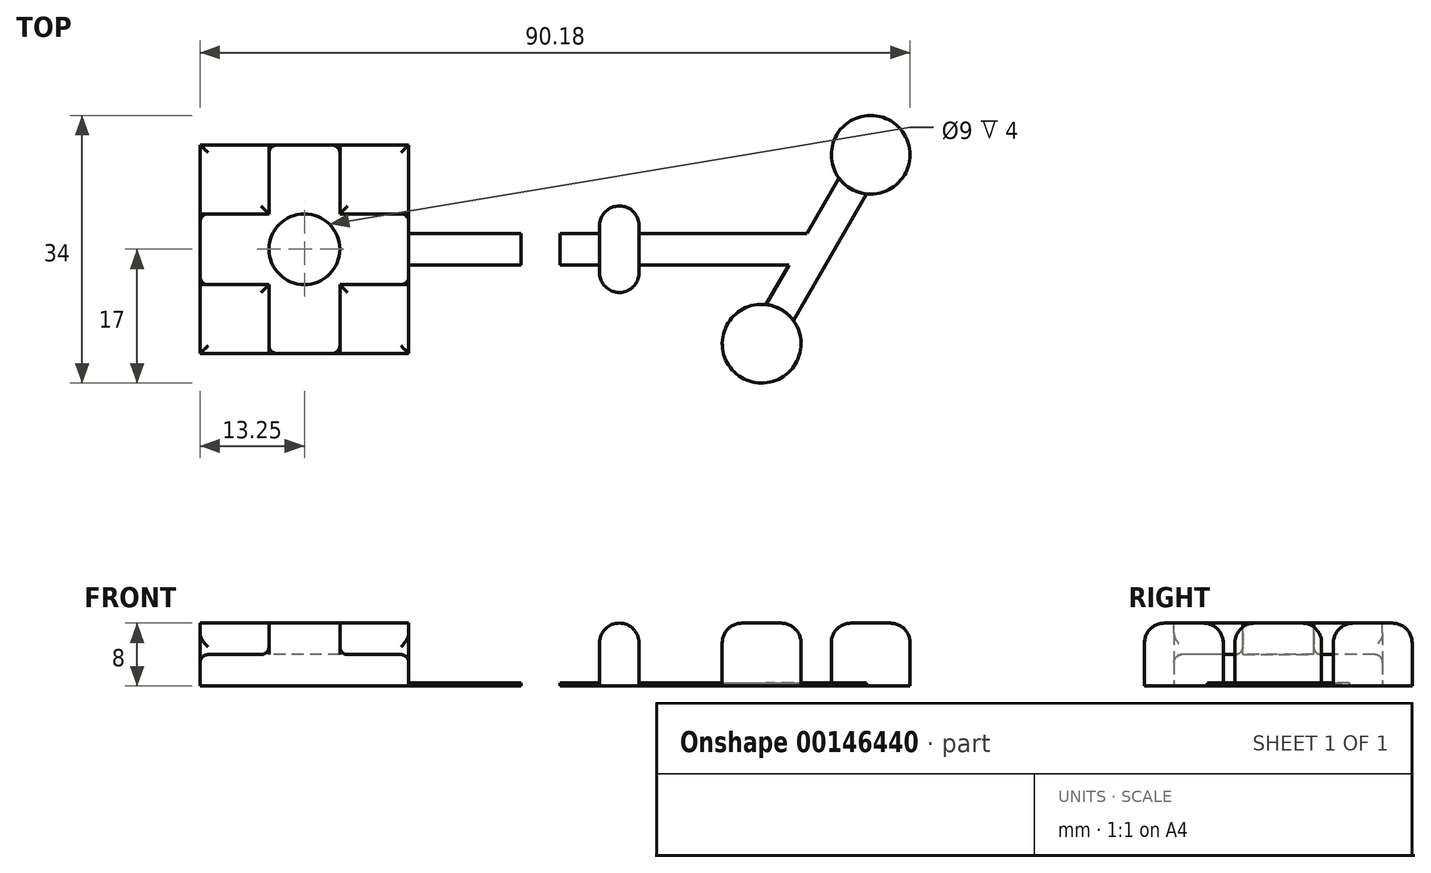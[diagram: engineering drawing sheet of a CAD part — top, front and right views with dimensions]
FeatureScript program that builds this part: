
annotation { "Feature Type Name" : "Feature", "Feature Type Description" : "" }
export const myFeature = defineFeature(function(context is Context, id is Id, definition is map)
    precondition{}
    {
        {
            var Q0;
            Q0=qCreatedBy(makeId("Top.planeOp"),FACE);
            var sketch = newSketch(context, id + "F0", { "sketchPlane" : qUnion([Q0])});
            skLineSegment(sketch, "E0.bottom", {"start": v(13.25, 13.25) * mm, "end": v(-13.25, 13.25) * mm});
            skLineSegment(sketch, "E0.top", {"start": v(13.25, -13.25) * mm, "end": v(-13.25, -13.25) * mm});
            skLineSegment(sketch, "E0.left", {"start": v(13.25, 13.25) * mm, "end": v(13.25, -13.25) * mm});
            skLineSegment(sketch, "E0.right", {"start": v(-13.25, 13.25) * mm, "end": v(-13.25, -13.25) * mm});
            skPoint(sketch, "E0.middle", {"position": v(0, 0) * mm});
            skLineSegment(sketch, "E1", {"start": v(0, 0) * mm, "end": v(65, 0) * mm, "construction": true});
            skLineSegment(sketch, "E2", {"start": v(58.07, -12) * mm, "end": v(71.93, 12) * mm, "construction": true});
            skPoint(sketch, "E3", {"position": v(58.07, -12) * mm});
            skCircle(sketch, "E4", {"center": v(71.93, 12) * mm, "radius": 5 * mm});
            skCircle(sketch, "E5", {"center": v(58.07, -12) * mm, "radius": 5 * mm});
            skLineSegment(sketch, "E6.bottom", {"start": v(32.5, -3) * mm, "end": v(27.5, -3) * mm, "construction": true});
            skLineSegment(sketch, "E6.top", {"start": v(32.5, 3) * mm, "end": v(27.5, 3) * mm, "construction": true});
            skLineSegment(sketch, "E6.left", {"start": v(32.5, -3) * mm, "end": v(32.5, 3) * mm});
            skLineSegment(sketch, "E6.right", {"start": v(27.5, -3) * mm, "end": v(27.5, 3) * mm});
            skPoint(sketch, "E6.middle", {"position": v(30, 0) * mm});
            skLineSegment(sketch, "E7.bottom", {"start": v(42.5, -3) * mm, "end": v(37.5, -3) * mm, "construction": true});
            skLineSegment(sketch, "E7.top", {"start": v(42.5, 3) * mm, "end": v(37.5, 3) * mm, "construction": true});
            skLineSegment(sketch, "E7.left", {"start": v(42.5, -3) * mm, "end": v(42.5, 3) * mm});
            skLineSegment(sketch, "E7.right", {"start": v(37.5, -3) * mm, "end": v(37.5, 3) * mm});
            skPoint(sketch, "E7.middle", {"position": v(40, 0) * mm});
            skArc(sketch, "E8", {"start": v(27.5, 3) * mm, "mid": v(30, 5.5) * mm, "end": v(32.5, 3) * mm});
            skArc(sketch, "E9", {"start": v(27.5, -3) * mm, "mid": v(30, -5.5) * mm, "end": v(32.5, -3) * mm});
            skArc(sketch, "E10", {"start": v(37.5, -3) * mm, "mid": v(40, -5.5) * mm, "end": v(42.5, -3) * mm});
            skArc(sketch, "E11", {"start": v(37.5, 3) * mm, "mid": v(40, 5.5) * mm, "end": v(42.5, 3) * mm});
            skLineSegment(sketch, "E12.0", {"start": v(58.63, -7.03) * mm, "end": v(67.9, 9.03) * mm});
            skLineSegment(sketch, "E13.MirrorCS", {"start": v(62.1, -9.03) * mm, "end": v(71.37, 7.03) * mm});
            skLineSegment(sketch, "E14", {"start": v(13.25, 2) * mm, "end": v(27.5, 2) * mm});
            skLineSegment(sketch, "E15", {"start": v(32.5, 2) * mm, "end": v(37.5, 2) * mm});
            skLineSegment(sketch, "E16", {"start": v(42.5, 2) * mm, "end": v(63.85, 2) * mm});
            skLineSegment(sketch, "E17.MirrorCS", {"start": v(13.25, -2) * mm, "end": v(27.5, -2) * mm});
            skLineSegment(sketch, "E18.MirrorCS", {"start": v(32.5, -2) * mm, "end": v(37.5, -2) * mm});
            skLineSegment(sketch, "E19.MirrorCS", {"start": v(42.5, -2) * mm, "end": v(61.54, -2) * mm});
            skPoint(sketch, "E20.orphan", {"position": v(63.85, -2) * mm});
            skSolve(sketch);
        }
        {
            var Q0;
            {var subQ3=sQuery(id+"F0.wireOp",EDGE,"E0.bottom");Q0=makeQuery(id+"F0.imprint","IMPRINT",FACE,{"disambiguationData":[TD([[makeQuery(id+"F0.imprint","IMPRINT",EDGE,{"derivedFrom":subQ3}),1.0]])]});}
            var Q1;
            {var subQ0=sQuery(id+"F0.wireOp",EDGE,"E4");var subQ1=makeQuery(id+"F0.imprint","INTERSECT",VERTEX,{"derivedFrom":[subQ0,sQuery(id+"F0.wireOp",EDGE,"E12.0")]});Q1=makeQuery(id+"F0.imprint","IMPRINT",FACE,{"disambiguationData":[TD([[makeQuery(id+"F0.imprint","IMPRINT",EDGE,{"disambiguationData":[TD([[subQ1,-1.0]])],"derivedFrom":subQ0}),1.0]])]});}
            var Q2;
            {var subQ0=sQuery(id+"F0.wireOp",EDGE,"E5");var subQ1=makeQuery(id+"F0.imprint","INTERSECT",VERTEX,{"derivedFrom":[subQ0,sQuery(id+"F0.wireOp",EDGE,"E12.0")]});Q2=makeQuery(id+"F0.imprint","IMPRINT",FACE,{"disambiguationData":[TD([[makeQuery(id+"F0.imprint","IMPRINT",EDGE,{"disambiguationData":[TD([[subQ1,1.0]])],"derivedFrom":subQ0}),1.0]])]});}
            var Q3;
            {var subQ3=sQuery(id+"F0.wireOp",EDGE,"E8");Q3=makeQuery(id+"F0.imprint","IMPRINT",FACE,{"disambiguationData":[TD([[makeQuery(id+"F0.imprint","IMPRINT",EDGE,{"derivedFrom":subQ3}),-1.0]])]});}
            var Q4;
            {var subQ0=sQuery(id+"F0.wireOp",EDGE,"E10");Q4=makeQuery(id+"F0.imprint","IMPRINT",FACE,{"disambiguationData":[TD([[makeQuery(id+"F0.imprint","IMPRINT",EDGE,{"derivedFrom":subQ0}),1.0]])]});}
            extrude(context, id + "F1", {"entities" : qUnion([Q0, Q1, Q2, Q3, Q4]), "depth" : 8 * mm});
        }
        {
            var Q0;
            {var subQ0=sQuery(id+"F0.wireOp",EDGE,"E14");Q0=makeQuery(id+"F0.imprint","IMPRINT",FACE,{"disambiguationData":[TD([[makeQuery(id+"F0.imprint","IMPRINT",EDGE,{"derivedFrom":subQ0}),-1.0]])]});}
            var Q1;
            {var subQ0=sQuery(id+"F0.wireOp",EDGE,"E15");Q1=makeQuery(id+"F0.imprint","IMPRINT",FACE,{"disambiguationData":[TD([[makeQuery(id+"F0.imprint","IMPRINT",EDGE,{"derivedFrom":subQ0}),-1.0]])]});}
            var Q2;
            {var subQ0=sQuery(id+"F0.wireOp",EDGE,"E16");Q2=makeQuery(id+"F0.imprint","IMPRINT",FACE,{"disambiguationData":[TD([[makeQuery(id+"F0.imprint","IMPRINT",EDGE,{"derivedFrom":subQ0}),-1.0]])]});}
            var Q3;
            {var subQ5=sQuery(id+"F0.wireOp",EDGE,"E13.MirrorCS");Q3=makeQuery(id+"F0.imprint","IMPRINT",FACE,{"disambiguationData":[TD([[makeQuery(id+"F0.imprint","IMPRINT",EDGE,{"derivedFrom":subQ5}),1.0]])]});}
            extrude(context, id + "F2", {"entities" : qUnion([Q0, Q1, Q2, Q3]), "operationType" : NewBodyOperationType.ADD, "depth" : 0.4 * mm});
        }
        {
            var Q0;
            Q0=makeQuery(id+"F1.opExtrude","CAP_FACE",FACE,{"disambiguationData":[OSD([sQuery(id+"F0.wireOp",EDGE,"E5")])],"isStart":false});
            var Q1;
            Q1=makeQuery(id+"F1.opExtrude","CAP_FACE",FACE,{"disambiguationData":[OSD([sQuery(id+"F0.wireOp",EDGE,"E4")])],"isStart":false});
            var Q2;
            Q2=makeQuery(id+"F1.opExtrude","CAP_FACE",FACE,{"disambiguationData":[OSD([sQuery(id+"F0.wireOp",EDGE,"E7.left"),sQuery(id+"F0.wireOp",EDGE,"E7.right"),sQuery(id+"F0.wireOp",EDGE,"E10"),sQuery(id+"F0.wireOp",EDGE,"E11")])],"isStart":false});
            var Q3;
            Q3=makeQuery(id+"F1.opExtrude","CAP_FACE",FACE,{"disambiguationData":[OSD([sQuery(id+"F0.wireOp",EDGE,"E6.left"),sQuery(id+"F0.wireOp",EDGE,"E6.right"),sQuery(id+"F0.wireOp",EDGE,"E8"),sQuery(id+"F0.wireOp",EDGE,"E9")])],"isStart":false});
            fillet(context, id + "F3", {"entities" : qUnion([Q0, Q1, Q2, Q3]), "radius" : 2.5 * mm, "tangentPropagation" : true, "allowEdgeOverflow" : false});
        }
        {
            var Q0;
            Q0=makeQuery(id+"F1.opExtrude","CAP_FACE",FACE,{"disambiguationData":[OSD([sQuery(id+"F0.wireOp",EDGE,"E0.bottom"),sQuery(id+"F0.wireOp",EDGE,"E0.top"),sQuery(id+"F0.wireOp",EDGE,"E0.left"),sQuery(id+"F0.wireOp",EDGE,"E0.right")])],"isStart":false});
            var sketch = newSketch(context, id + "F4", { "sketchPlane" : qUnion([Q0])});
            skCircle(sketch, "E21", {"center": v(0, 0) * mm, "radius": 4.5 * mm});
            skLineSegment(sketch, "E22", {"start": v(-4.5, 13.25) * mm, "end": v(-4.5, 4.5) * mm});
            skLineSegment(sketch, "E23", {"start": v(4.5, 13.25) * mm, "end": v(4.5, 4.5) * mm});
            skLineSegment(sketch, "E24", {"start": v(-13.25, 4.5) * mm, "end": v(-4.5, 4.5) * mm});
            skLineSegment(sketch, "E25", {"start": v(-13.25, -4.5) * mm, "end": v(-4.5, -4.5) * mm});
            skLineSegment(sketch, "E26.trimOffspring", {"start": v(4.5, 4.5) * mm, "end": v(13.25, 4.5) * mm});
            skLineSegment(sketch, "E27.trimOffspring", {"start": v(-4.5, -4.5) * mm, "end": v(-4.5, -13.25) * mm});
            skLineSegment(sketch, "E28.trimOffspring", {"start": v(4.5, -4.5) * mm, "end": v(13.25, -4.5) * mm});
            skLineSegment(sketch, "E29.trimOffspring", {"start": v(4.5, -4.5) * mm, "end": v(4.5, -13.25) * mm});
            skSolve(sketch);
        }
        {
            var Q0;
            Q0=makeQuery(id+"F4.imprint","IMPRINT",FACE,{"disambiguationData":[TD([[makeQuery(id+"F4.imprint","IMPRINT",EDGE,{"derivedFrom":sQuery(id+"F4.wireOp",EDGE,"E21")}),1.0]])]});
            var Q1;
            {var subQ0=sQuery(id+"F4.wireOp",EDGE,"E22");Q1=makeQuery(id+"F4.imprint","IMPRINT",FACE,{"disambiguationData":[TD([[makeQuery(id+"F4.imprint","IMPRINT",EDGE,{"derivedFrom":subQ0}),-1.0]])]});}
            var Q2;
            {var subQ0=sQuery(id+"F4.wireOp",EDGE,"E25");Q2=makeQuery(id+"F4.imprint","IMPRINT",FACE,{"disambiguationData":[TD([[makeQuery(id+"F4.imprint","IMPRINT",EDGE,{"derivedFrom":subQ0}),-1.0]])]});}
            var Q3;
            {var subQ0=sQuery(id+"F4.wireOp",EDGE,"E28.trimOffspring");Q3=makeQuery(id+"F4.imprint","IMPRINT",FACE,{"disambiguationData":[TD([[makeQuery(id+"F4.imprint","IMPRINT",EDGE,{"derivedFrom":subQ0}),-1.0]])]});}
            var Q4;
            {var subQ0=sQuery(id+"F4.wireOp",EDGE,"E23");Q4=makeQuery(id+"F4.imprint","IMPRINT",FACE,{"disambiguationData":[TD([[makeQuery(id+"F4.imprint","IMPRINT",EDGE,{"derivedFrom":subQ0}),1.0]])]});}
            extrude(context, id + "F5", {"entities" : qUnion([Q0, Q1, Q2, Q3, Q4]), "operationType" : NewBodyOperationType.REMOVE, "oppositeDirection" : true, "depth" : 4 * mm});
        }
        {
            var Q0;
            Q0=makeQuery(id+"F5.boolean.opBoolean","COPY",FACE,{"derivedFrom":makeQuery(id+"F5.opExtrude","CAP_FACE",FACE,{"disambiguationData":[OSD([sQuery(id+"F0.wireOp",EDGE,"E0.top"),sQuery(id+"F0.wireOp",EDGE,"E0.left"),sQuery(id+"F4.wireOp",EDGE,"E28.trimOffspring"),sQuery(id+"F4.wireOp",EDGE,"E29.trimOffspring")])],"isStart":false})});
            var Q1;
            Q1=makeQuery(id+"F5.boolean.opBoolean","COPY",FACE,{"derivedFrom":makeQuery(id+"F5.opExtrude","CAP_FACE",FACE,{"disambiguationData":[OSD([sQuery(id+"F0.wireOp",EDGE,"E0.bottom"),sQuery(id+"F0.wireOp",EDGE,"E0.left"),sQuery(id+"F4.wireOp",EDGE,"E23"),sQuery(id+"F4.wireOp",EDGE,"E26.trimOffspring")])],"isStart":false})});
            var Q2;
            Q2=makeQuery(id+"F5.boolean.opBoolean","COPY",FACE,{"derivedFrom":makeQuery(id+"F5.opExtrude","CAP_FACE",FACE,{"disambiguationData":[OSD([sQuery(id+"F0.wireOp",EDGE,"E0.bottom"),sQuery(id+"F0.wireOp",EDGE,"E0.right"),sQuery(id+"F4.wireOp",EDGE,"E22"),sQuery(id+"F4.wireOp",EDGE,"E24")])],"isStart":false})});
            var Q3;
            Q3=makeQuery(id+"F5.boolean.opBoolean","COPY",FACE,{"derivedFrom":makeQuery(id+"F5.opExtrude","CAP_FACE",FACE,{"disambiguationData":[OSD([sQuery(id+"F0.wireOp",EDGE,"E0.top"),sQuery(id+"F0.wireOp",EDGE,"E0.right"),sQuery(id+"F4.wireOp",EDGE,"E25"),sQuery(id+"F4.wireOp",EDGE,"E27.trimOffspring")])],"isStart":false})});
            fillet(context, id + "F6", {"entities" : qUnion([Q0, Q1, Q2, Q3]), "radius" : 1 * mm, "tangentPropagation" : true, "allowEdgeOverflow" : false});
        }
    });
